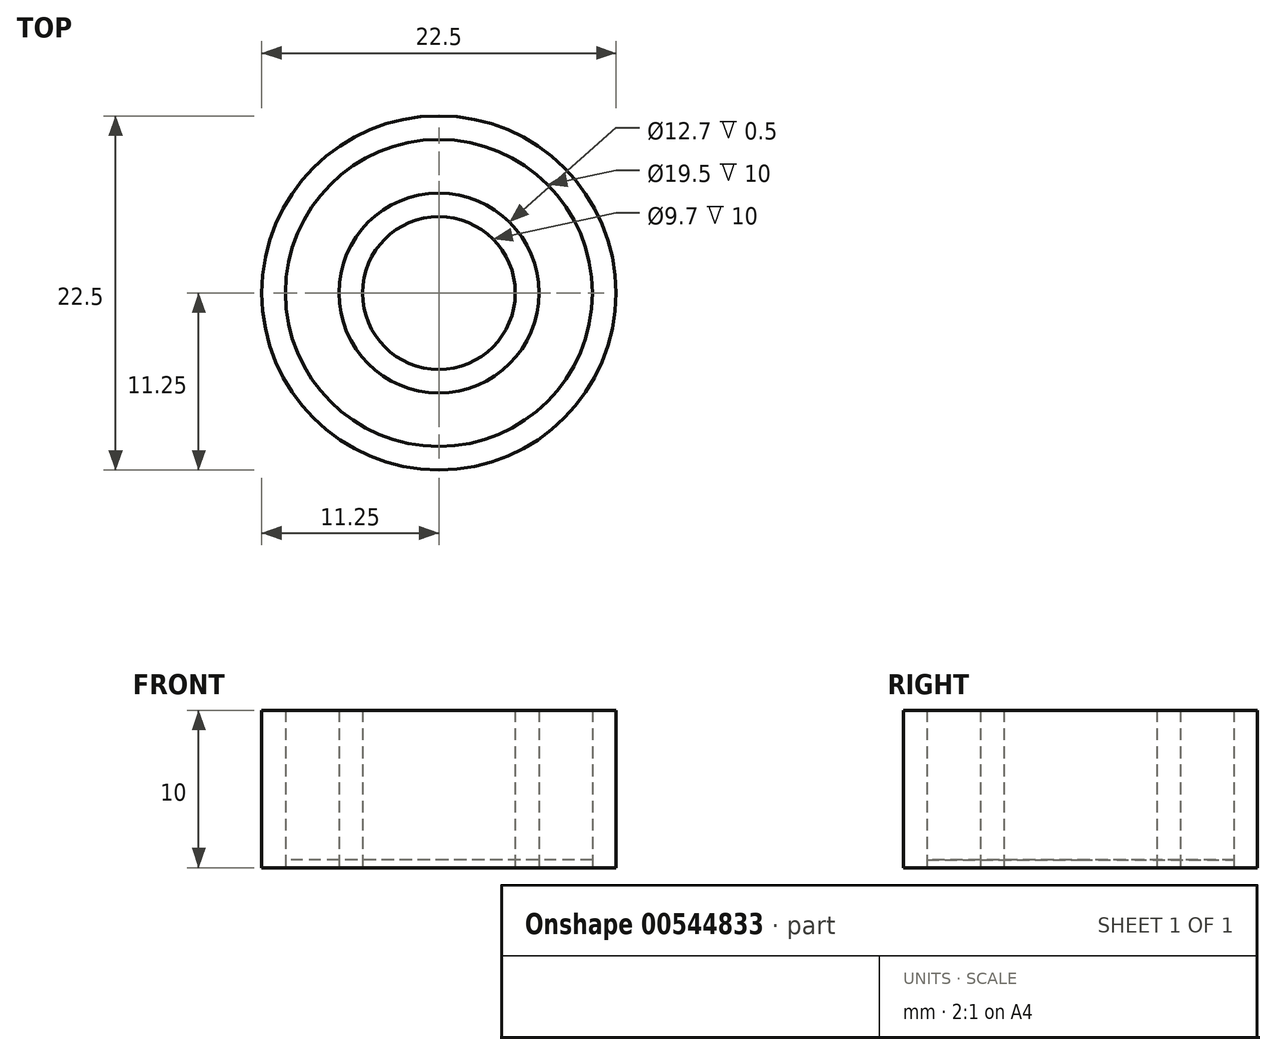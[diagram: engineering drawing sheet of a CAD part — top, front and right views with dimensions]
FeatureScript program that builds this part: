
annotation { "Feature Type Name" : "Feature", "Feature Type Description" : "" }
export const myFeature = defineFeature(function(context is Context, id is Id, definition is map)
    precondition{}
    {
        {
            var Q0;
            Q0=qCreatedBy(makeId("Top.planeOp"),FACE);
            var sketch = newSketch(context, id + "F0", { "sketchPlane" : qUnion([Q0])});
            skCircle(sketch, "E0", {"center": v(0, 0) * mm, "radius": 9.75 * mm});
            skCircle(sketch, "E1", {"center": v(0, 0) * mm, "radius": 6.35 * mm});
            skCircle(sketch, "E2.0", {"center": v(0, 0) * mm, "radius": 11.25 * mm});
            skCircle(sketch, "E3.0", {"center": v(0, 0) * mm, "radius": 4.85 * mm});
            skSolve(sketch);
        }
        {
            var Q0;
            Q0=makeQuery(id+"F0.imprint","IMPRINT",FACE,{"disambiguationData":[TD([[makeQuery(id+"F0.imprint","IMPRINT",EDGE,{"derivedFrom":sQuery(id+"F0.wireOp",EDGE,"E0")}),-1.0]])]});
            var Q1;
            Q1=makeQuery(id+"F0.imprint","IMPRINT",FACE,{"disambiguationData":[TD([[makeQuery(id+"F0.imprint","IMPRINT",EDGE,{"derivedFrom":sQuery(id+"F0.wireOp",EDGE,"E1")}),1.0]])]});
            extrude(context, id + "F1", {"entities" : qUnion([Q0, Q1]), "depth" : 10 * mm, "offsetDistance" : 25 * mm});
        }
        {
            var Q0;
            Q0=makeQuery(id+"F0.imprint","IMPRINT",FACE,{"disambiguationData":[TD([[makeQuery(id+"F0.imprint","IMPRINT",EDGE,{"derivedFrom":sQuery(id+"F0.wireOp",EDGE,"E0")}),1.0]])]});
            extrude(context, id + "F2", {"entities" : qUnion([Q0]), "depth" : 0.5 * mm, "offsetDistance" : 25 * mm});
        }
    });
